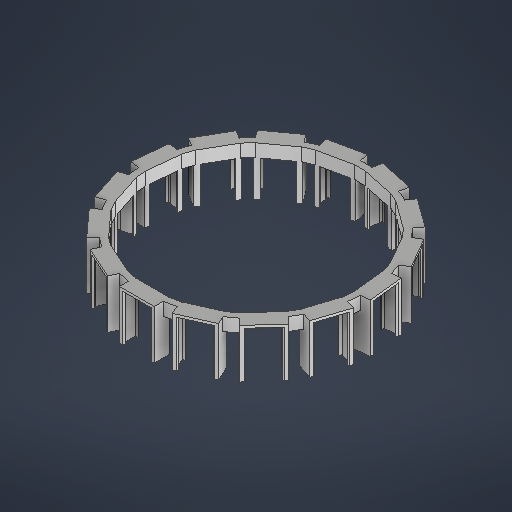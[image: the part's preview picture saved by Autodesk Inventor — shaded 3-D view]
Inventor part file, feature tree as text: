
AUTODESK INVENTOR PART (.ipt)
format: ipt  version: 2025.1 (Build 291241020, 241B)  size: 537,088 bytes
history: native  units: mm
features: extrude x4, sketch x3, chamfer x1, pattern_circular x1, projected_geometry x1
ambient origin geometry x8: Origin, YZ Plane, XZ Plane, XY Plane, X Axis, Y Axis, Z Axis, Center Point
bodies: Solid1 (feature_tree)
feature tree (10):
  extrude  "Extrusion1"  Depth=5.0mm
  extrude  "Extrusion2"  Depth=27.0mm
  sketch  "Sketch4"  dims[d5=12.0mm d6=38.0mm d7=0.0mm d8=25.0mm d9=1.9mm d10=1.0mm d11=24.0mm d12=1.0mm d13=20.0mm d14=36.0mm d15=0.0mm d16=1.0mm d17=2.0mm d18=45.0deg d19=150.0mm d20=360.0deg d22=20.0mm d23=28.0mm d24=0.0mm]
  extrude  "Extrusion3"  Depth=38.0mm TaperAngle=0.0deg
  extrude  "Extrusion4"  Depth=25.0mm
  chamfer  "Chamfer1"  Distance=1.9mm
  pattern_circular  "Circular Pattern1"  [2 undecoded]
  sketch  "Sketch1"  dims[d0=162.0mm d1=5.0mm]
  sketch  "Sketch3"  dims[d2=10.0mm d3=0.0mm d4=27.0mm]
  projected_geometry  "Projected Loop1"
note: 2 required parameter values undecoded (feature->parameter linkage not recoverable at this tier; creation-order binding heuristic only, values carry confidence <= 0.55)
